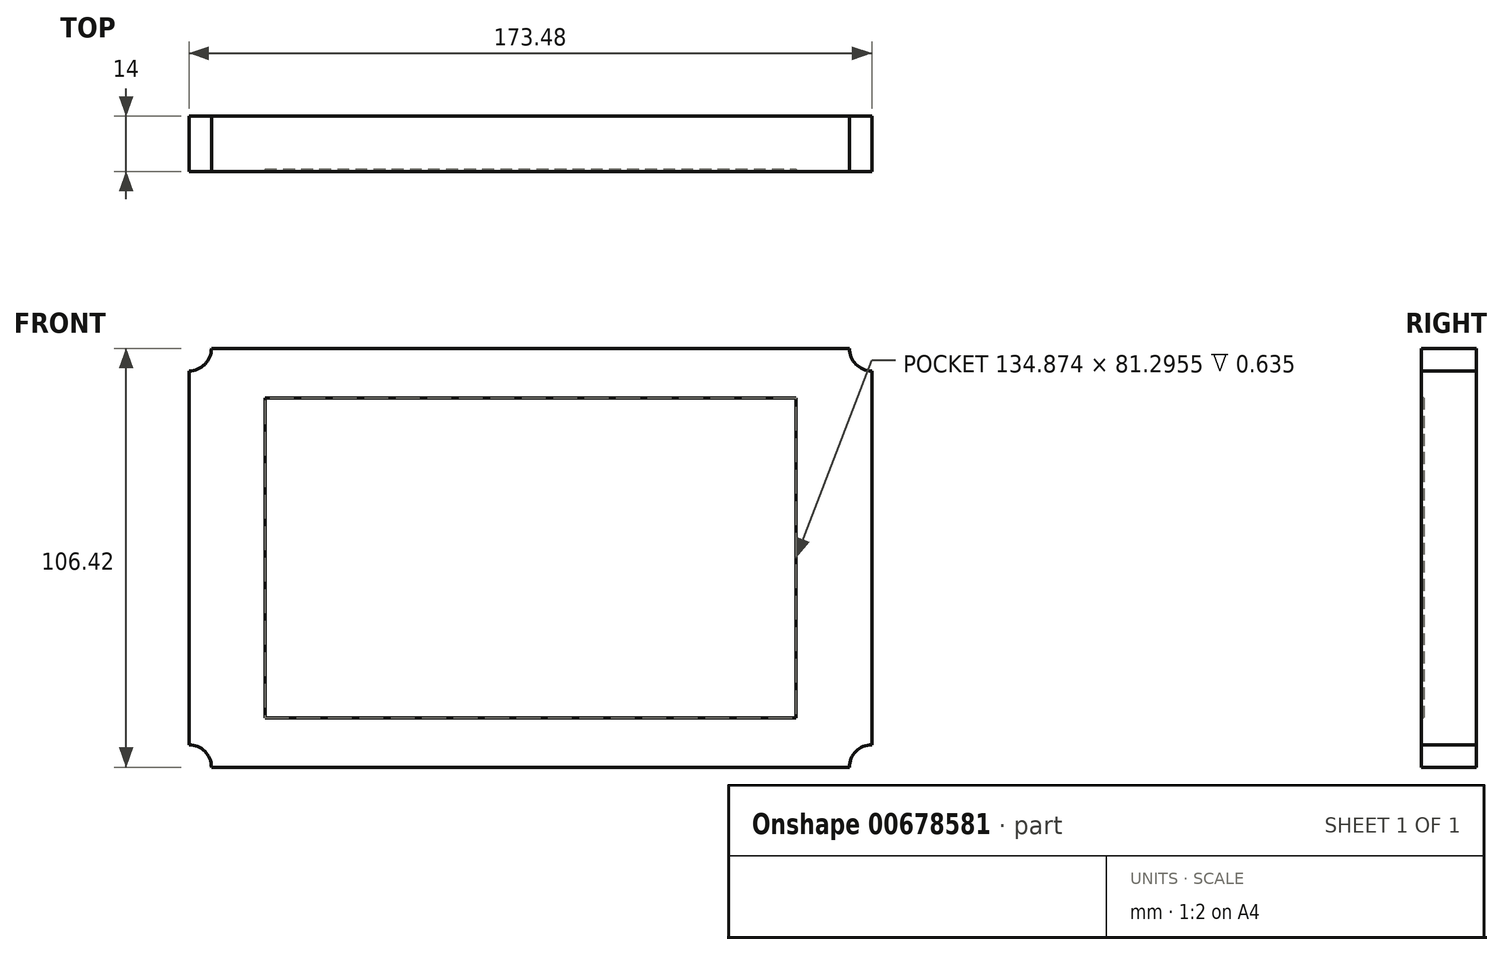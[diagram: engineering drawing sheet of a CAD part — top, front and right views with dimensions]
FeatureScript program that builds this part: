
annotation { "Feature Type Name" : "Feature", "Feature Type Description" : "" }
export const myFeature = defineFeature(function(context is Context, id is Id, definition is map)
    precondition{}
    {
        {
            var Q0;
            Q0=qCreatedBy(makeId("Front.planeOp"),FACE);
            var sketch = newSketch(context, id + "F0", { "sketchPlane" : qUnion([Q0])});
            skLineSegment(sketch, "E0.bottom", {"start": v(-76.9, 80.93) * mm, "end": v(96.58, 80.93) * mm});
            skLineSegment(sketch, "E0.top", {"start": v(-76.9, -25.5) * mm, "end": v(96.58, -25.5) * mm});
            skLineSegment(sketch, "E0.left", {"start": v(-76.9, 80.93) * mm, "end": v(-76.9, -25.5) * mm});
            skLineSegment(sketch, "E0.right", {"start": v(96.58, 80.93) * mm, "end": v(96.58, -25.5) * mm});
            skSolve(sketch);
        }
        {
            var Q0;
            Q0=makeQuery(id+"F0.imprint","IMPRINT",FACE,{"disambiguationData":[TD([[makeQuery(id+"F0.imprint","IMPRINT",EDGE,{"derivedFrom":sQuery(id+"F0.wireOp",EDGE,"E0.bottom")}),-1.0]])]});
            extrude(context, id + "F1", {"entities" : qUnion([Q0]), "depth" : 14 * mm, "offsetDistance" : 25.4 * mm});
        }
        {
            var Q0;
            Q0=makeQuery(id+"F1.opExtrude","CAP_FACE",FACE,{"disambiguationData":[OSD([sQuery(id+"F0.wireOp",EDGE,"E0.bottom"),sQuery(id+"F0.wireOp",EDGE,"E0.top"),sQuery(id+"F0.wireOp",EDGE,"E0.left"),sQuery(id+"F0.wireOp",EDGE,"E0.right")])],"isStart":false});
            var sketch = newSketch(context, id + "F2", { "sketchPlane" : qUnion([Q0])});
            skLineSegment(sketch, "E1.bottom", {"start": v(-57.6, 68.36) * mm, "end": v(77.28, 68.36) * mm});
            skLineSegment(sketch, "E1.top", {"start": v(-57.6, -12.93) * mm, "end": v(77.28, -12.93) * mm});
            skLineSegment(sketch, "E1.left", {"start": v(-57.6, 68.36) * mm, "end": v(-57.6, -12.93) * mm});
            skLineSegment(sketch, "E1.right", {"start": v(77.28, 68.36) * mm, "end": v(77.28, -12.93) * mm});
            skSolve(sketch);
        }
        {
            var Q0;
            Q0=makeQuery(id+"F2.imprint","IMPRINT",FACE,{"disambiguationData":[TD([[makeQuery(id+"F2.imprint","IMPRINT",EDGE,{"derivedFrom":sQuery(id+"F2.wireOp",EDGE,"E1.bottom")}),-1.0]])]});
            extrude(context, id + "F3", {"entities" : qUnion([Q0]), "operationType" : NewBodyOperationType.REMOVE, "oppositeDirection" : true, "depth" : 0.64 * mm, "offsetDistance" : 25.4 * mm});
        }
        {
            var Q0;
            Q0=makeQuery(id+"F1.opExtrude","CAP_FACE",FACE,{"disambiguationData":[OSD([sQuery(id+"F0.wireOp",EDGE,"E0.bottom"),sQuery(id+"F0.wireOp",EDGE,"E0.top"),sQuery(id+"F0.wireOp",EDGE,"E0.left"),sQuery(id+"F0.wireOp",EDGE,"E0.right")])],"isStart":false});
            var sketch = newSketch(context, id + "F4", { "sketchPlane" : qUnion([Q0])});
            skCircle(sketch, "E2", {"center": v(-76.9, 80.93) * mm, "radius": 5.72 * mm});
            skCircle(sketch, "E3", {"center": v(-76.9, -25.5) * mm, "radius": 5.72 * mm});
            skCircle(sketch, "E4", {"center": v(96.58, -25.5) * mm, "radius": 5.72 * mm});
            skCircle(sketch, "E5", {"center": v(96.58, 80.93) * mm, "radius": 5.72 * mm});
            skSolve(sketch);
        }
        {
            var Q0;
            {var subQ0=sQuery(id+"F4.wireOp",EDGE,"E2");var subQ1=makeQuery(id+"F1.opExtrude","CAP_EDGE",EDGE,{"disambiguationData":[OSD([sQuery(id+"F0.wireOp",EDGE,"E0.bottom")])],"isStart":false});var subQ2=makeQuery(id+"F4.imprint","INTERSECT",VERTEX,{"derivedFrom":[subQ1,subQ0]});Q0=makeQuery(id+"F4.imprint","IMPRINT",FACE,{"disambiguationData":[TD([[makeQuery(id+"F4.imprint","IMPRINT",EDGE,{"disambiguationData":[TD([[subQ2,1.0]])],"derivedFrom":subQ0}),1.0]])]});}
            var Q1;
            {var subQ0=sQuery(id+"F4.wireOp",EDGE,"E3");var subQ1=makeQuery(id+"F1.opExtrude","CAP_EDGE",EDGE,{"disambiguationData":[OSD([sQuery(id+"F0.wireOp",EDGE,"E0.top")])],"isStart":false});var subQ2=makeQuery(id+"F4.imprint","INTERSECT",VERTEX,{"derivedFrom":[subQ1,subQ0]});Q1=makeQuery(id+"F4.imprint","IMPRINT",FACE,{"disambiguationData":[TD([[makeQuery(id+"F4.imprint","IMPRINT",EDGE,{"disambiguationData":[TD([[subQ2,-1.0]])],"derivedFrom":subQ0}),1.0]])]});}
            var Q2;
            {var subQ0=sQuery(id+"F4.wireOp",EDGE,"E4");var subQ1=makeQuery(id+"F1.opExtrude","CAP_EDGE",EDGE,{"disambiguationData":[OSD([sQuery(id+"F0.wireOp",EDGE,"E0.top")])],"isStart":false});var subQ2=makeQuery(id+"F4.imprint","INTERSECT",VERTEX,{"derivedFrom":[subQ1,subQ0]});Q2=makeQuery(id+"F4.imprint","IMPRINT",FACE,{"disambiguationData":[TD([[makeQuery(id+"F4.imprint","IMPRINT",EDGE,{"disambiguationData":[TD([[subQ2,1.0]])],"derivedFrom":subQ0}),1.0]])]});}
            var Q3;
            {var subQ0=sQuery(id+"F4.wireOp",EDGE,"E5");var subQ1=makeQuery(id+"F1.opExtrude","CAP_EDGE",EDGE,{"disambiguationData":[OSD([sQuery(id+"F0.wireOp",EDGE,"E0.bottom")])],"isStart":false});var subQ2=makeQuery(id+"F4.imprint","INTERSECT",VERTEX,{"derivedFrom":[subQ1,subQ0]});Q3=makeQuery(id+"F4.imprint","IMPRINT",FACE,{"disambiguationData":[TD([[makeQuery(id+"F4.imprint","IMPRINT",EDGE,{"disambiguationData":[TD([[subQ2,-1.0]])],"derivedFrom":subQ0}),1.0]])]});}
            extrude(context, id + "F5", {"entities" : qUnion([Q0, Q1, Q2, Q3]), "operationType" : NewBodyOperationType.REMOVE, "oppositeDirection" : true, "depth" : 25.4 * mm, "offsetDistance" : 25.4 * mm});
        }
    });
